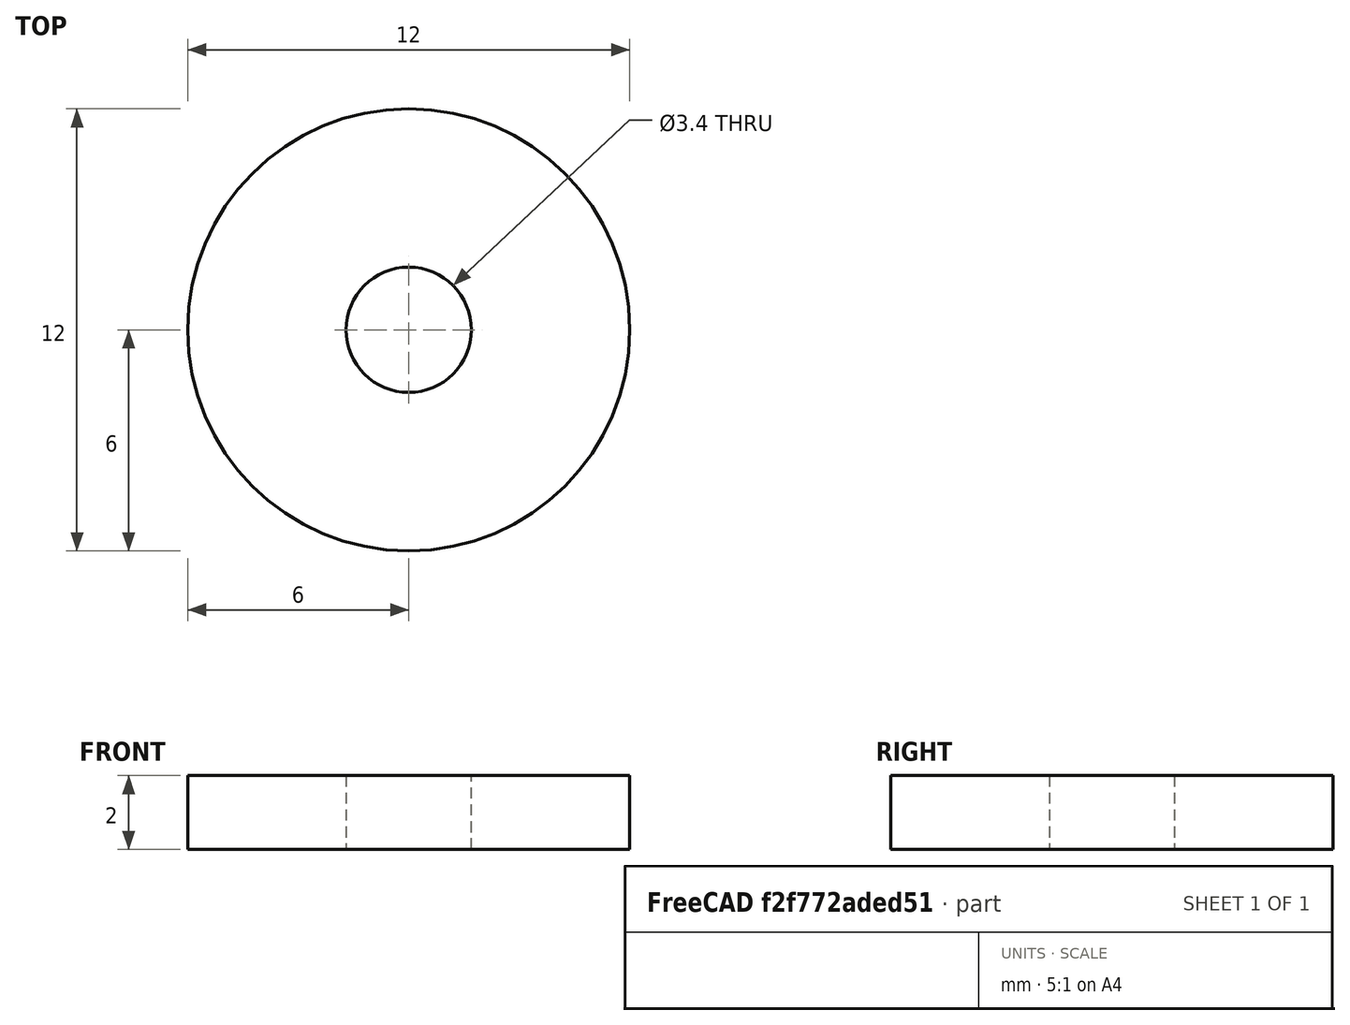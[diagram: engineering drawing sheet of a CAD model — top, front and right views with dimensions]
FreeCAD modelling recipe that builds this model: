
FCSTD DOCUMENT  (FreeCAD 0.19R24291 (Git))
Label: Gear02Cap
License: All rights reserved
LicenseURL: http://en.wikipedia.org/wiki/All_rights_reserved
objects: PartDesign::CoordinateSystem×2, Sketcher::SketchObject×1, PartDesign::Pad×1, PartDesign::Body×1
note: 6 computed .brp shape members not serialized (recipe doc carries the construction recipe); baked Part::Feature solids carry a one-line shape summary decoded from their .brp
EXTERNAL_REF file=data.FCStd obj=Spreadsheet

FEATURE [PartDesign::CoordinateSystem] LCS_0
  AttacherType = Attacher::AttachEngine3D
  MapMode = 2
  Support = -> [X_Axis]
FEATURE [Sketcher::SketchObject] Sketch
  FullyConstrained = true
  MapMode = 5
  Support = -> [XY_Plane]
  expr: Constraints[2] = data#<<data>>.M3DiameterHole
  expr: Constraints[3] = data#<<data>>.Gear02ShaftDiameter * 2
  sketch-geometry (2):
    g0: Circle CenterX=0 CenterY=0 CenterZ=0 NormalX=0 NormalY=0 NormalZ=1 AngleXU=0 Radius=6
    g1: Circle CenterX=0 CenterY=0 CenterZ=0 NormalX=0 NormalY=0 NormalZ=1 AngleXU=0 Radius=1.7
  constraints (4):
    c: Coincident(g0,g-1)
    c: Coincident(g1,g0)
    c: Diameter(g1) = 3.4
    c: Diameter(g0) = 12
FEATURE [PartDesign::Pad] Pad
  Direction = (1,1,1)
  Length = 2
  Length2 = 100
  Profile = -> Sketch
  Type = 0
  expr: Length = data#<<data>>.HallSensorGap
FEATURE [PartDesign::CoordinateSystem] LCS_pcb
  AttacherType = Attacher::AttachEngine3D
  MapMode = 11
  Placement = pos=(0,0,2) rot=(0,0,1;1.5708rad)
  Support = -> [Pad]
FEATURE [PartDesign::Body] Body_gear02cap
  Group = -> [LCS_0,Sketch,Pad,LCS_pcb]
  Origin = -> Origin
  Tip = -> Pad
